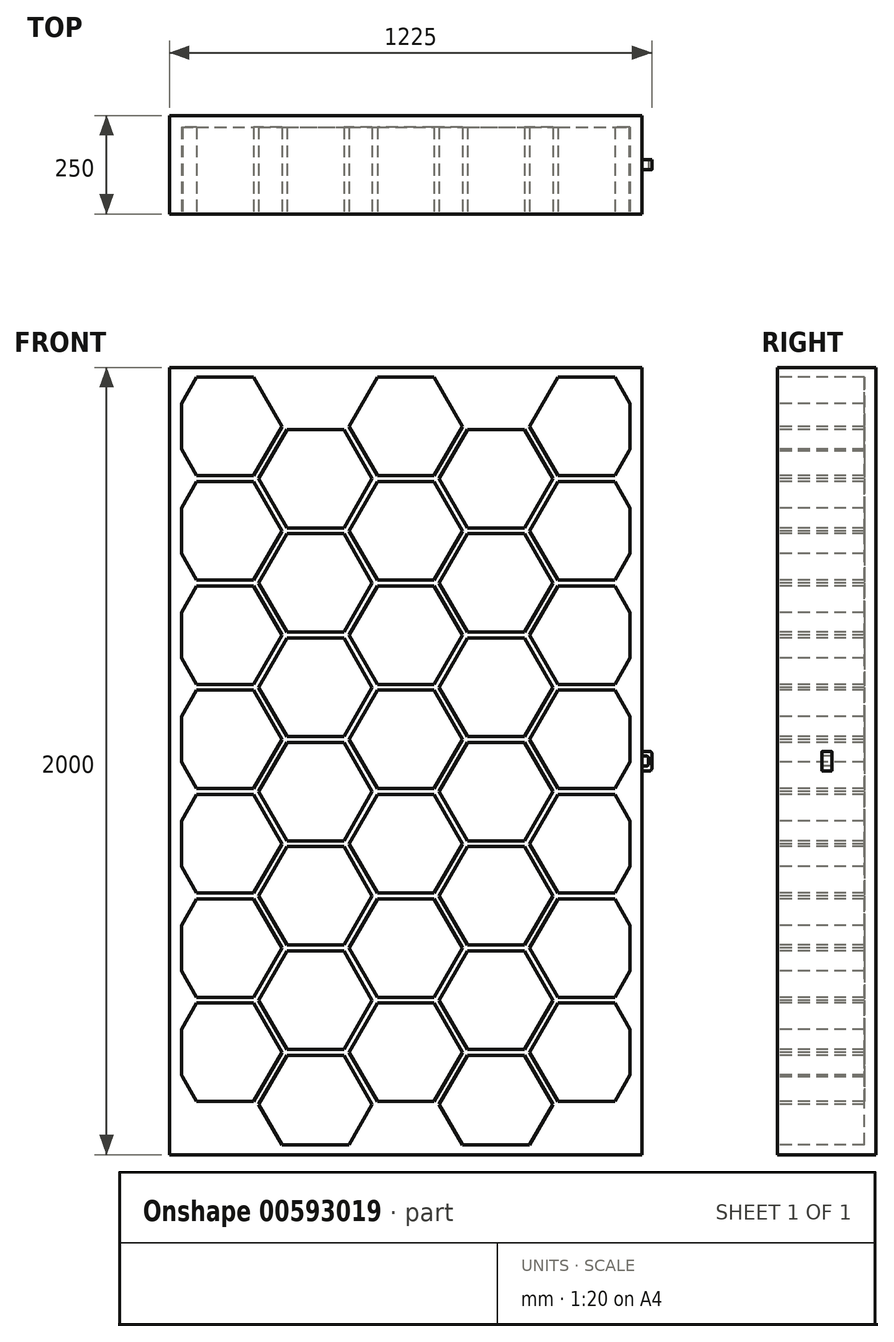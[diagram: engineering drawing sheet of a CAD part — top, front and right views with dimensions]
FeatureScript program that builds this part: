
annotation { "Feature Type Name" : "Feature", "Feature Type Description" : "" }
export const myFeature = defineFeature(function(context is Context, id is Id, definition is map)
    precondition{}
    {
        {
            var Q0;
            Q0=qCreatedBy(makeId("Top.planeOp"),FACE);
            var sketch = newSketch(context, id + "F0", { "sketchPlane" : qUnion([Q0])});
            skLineSegment(sketch, "E0.bottom", {"start": v(0, 0) * mm, "end": v(1200, 0) * mm});
            skLineSegment(sketch, "E0.top", {"start": v(0, 250) * mm, "end": v(1200, 250) * mm});
            skLineSegment(sketch, "E0.left", {"start": v(0, 0) * mm, "end": v(0, 250) * mm});
            skLineSegment(sketch, "E0.right", {"start": v(1200, 0) * mm, "end": v(1200, 250) * mm});
            skSolve(sketch);
        }
        {
            var Q0;
            Q0 = qSketchRegion(id + "F0", true);
            extrude(context, id + "F1", {"entities" : qUnion([Q0]), "depth" : 2000 * mm, "offsetDistance" : 25 * mm});
        }
        {
            var Q0;
            Q0=makeQuery(id+"F1.opExtrude","CAP_FACE",FACE,{"disambiguationData":[OSD([sQuery(id+"F0.wireOp",EDGE,"E0.bottom"),sQuery(id+"F0.wireOp",EDGE,"E0.top"),sQuery(id+"F0.wireOp",EDGE,"E0.left"),sQuery(id+"F0.wireOp",EDGE,"E0.right")])],"isStart":false});
            cPlane(context, id + "F2", {"entities" : qUnion([Q0]), "cplaneType" : CPlaneType.OFFSET, "offset" : 1000 * mm, "oppositeDirection" : true, "width" : 150 * mm, "height" : 150 * mm});
        }
        {
            var Q0;
            Q0=makeQuery(id+"F1.opExtrude","SWEPT_FACE",FACE,{"disambiguationData":[OSD([sQuery(id+"F0.wireOp",EDGE,"E0.left")])]});
            cPlane(context, id + "F3", {"entities" : qUnion([Q0]), "cplaneType" : CPlaneType.OFFSET, "offset" : 600 * mm, "oppositeDirection" : true, "width" : 150 * mm, "height" : 150 * mm});
        }
        {
            var Q0;
            Q0=makeQuery(id+"F1.opExtrude","SWEPT_FACE",FACE,{"disambiguationData":[OSD([sQuery(id+"F0.wireOp",EDGE,"E0.bottom")])]});
            var sketch = newSketch(context, id + "F4", { "sketchPlane" : qUnion([Q0])});
            skCircle(sketch, "E1.cCircle", {"center": v(600, 1850) * mm, "radius": 125 * mm, "construction": true});
            skLineSegment(sketch, "E1.0", {"start": v(744.34, 1850) * mm, "end": v(672.17, 1725) * mm});
            skLineSegment(sketch, "E1.1", {"start": v(672.17, 1725) * mm, "end": v(527.83, 1725) * mm});
            skLineSegment(sketch, "E1.2", {"start": v(527.83, 1725) * mm, "end": v(455.66, 1850) * mm});
            skLineSegment(sketch, "E1.3", {"start": v(455.66, 1850) * mm, "end": v(527.83, 1975) * mm});
            skLineSegment(sketch, "E1.4", {"start": v(527.83, 1975) * mm, "end": v(672.17, 1975) * mm});
            skLineSegment(sketch, "E1.5", {"start": v(672.17, 1975) * mm, "end": v(744.34, 1850) * mm});
            skPoint(sketch, "E1.0.midPoint", {"position": v(708.25, 1787.5) * mm});
            skCircle(sketch, "E2.cCircle", {"center": v(829.5, 1717.5) * mm, "radius": 125 * mm, "construction": true});
            skLineSegment(sketch, "E2.0", {"start": v(973.83, 1717.5) * mm, "end": v(901.67, 1592.5) * mm});
            skLineSegment(sketch, "E2.1", {"start": v(901.67, 1592.5) * mm, "end": v(757.33, 1592.5) * mm});
            skLineSegment(sketch, "E2.2", {"start": v(757.33, 1592.5) * mm, "end": v(685.16, 1717.5) * mm});
            skLineSegment(sketch, "E2.3", {"start": v(685.16, 1717.5) * mm, "end": v(757.33, 1842.5) * mm});
            skLineSegment(sketch, "E2.4", {"start": v(757.33, 1842.5) * mm, "end": v(901.67, 1842.5) * mm});
            skLineSegment(sketch, "E2.5", {"start": v(901.67, 1842.5) * mm, "end": v(973.83, 1717.5) * mm});
            skPoint(sketch, "E2.0.midPoint", {"position": v(937.75, 1655) * mm});
            skCircle(sketch, "E3.cCircle", {"center": v(600, 1585) * mm, "radius": 125 * mm, "construction": true});
            skLineSegment(sketch, "E3.0", {"start": v(744.34, 1585) * mm, "end": v(672.17, 1460) * mm});
            skLineSegment(sketch, "E3.1", {"start": v(672.17, 1460) * mm, "end": v(527.83, 1460) * mm});
            skLineSegment(sketch, "E3.2", {"start": v(527.83, 1460) * mm, "end": v(455.66, 1585) * mm});
            skLineSegment(sketch, "E3.3", {"start": v(455.66, 1585) * mm, "end": v(527.83, 1710) * mm});
            skLineSegment(sketch, "E3.4", {"start": v(527.83, 1710) * mm, "end": v(672.17, 1710) * mm});
            skLineSegment(sketch, "E3.5", {"start": v(672.17, 1710) * mm, "end": v(744.34, 1585) * mm});
            skPoint(sketch, "E3.0.midPoint", {"position": v(708.25, 1522.5) * mm});
            skCircle(sketch, "E4.cCircle", {"center": v(370.5, 1717.5) * mm, "radius": 125 * mm, "construction": true});
            skLineSegment(sketch, "E4.0", {"start": v(514.84, 1717.5) * mm, "end": v(442.67, 1592.5) * mm});
            skLineSegment(sketch, "E4.1", {"start": v(442.67, 1592.5) * mm, "end": v(298.33, 1592.5) * mm});
            skLineSegment(sketch, "E4.2", {"start": v(298.33, 1592.5) * mm, "end": v(226.17, 1717.5) * mm});
            skLineSegment(sketch, "E4.3", {"start": v(226.17, 1717.5) * mm, "end": v(298.33, 1842.5) * mm});
            skLineSegment(sketch, "E4.4", {"start": v(298.33, 1842.5) * mm, "end": v(442.67, 1842.5) * mm});
            skLineSegment(sketch, "E4.5", {"start": v(442.67, 1842.5) * mm, "end": v(514.84, 1717.5) * mm});
            skPoint(sketch, "E4.0.midPoint", {"position": v(478.76, 1655) * mm});
            skCircle(sketch, "E5.cCircle", {"center": v(370.5, 1452.5) * mm, "radius": 125 * mm, "construction": true});
            skLineSegment(sketch, "E5.0", {"start": v(514.84, 1452.5) * mm, "end": v(442.67, 1327.5) * mm});
            skLineSegment(sketch, "E5.1", {"start": v(442.67, 1327.5) * mm, "end": v(298.33, 1327.5) * mm});
            skLineSegment(sketch, "E5.2", {"start": v(298.33, 1327.5) * mm, "end": v(226.17, 1452.5) * mm});
            skLineSegment(sketch, "E5.3", {"start": v(226.17, 1452.5) * mm, "end": v(298.33, 1577.5) * mm});
            skLineSegment(sketch, "E5.4", {"start": v(298.33, 1577.5) * mm, "end": v(442.67, 1577.5) * mm});
            skLineSegment(sketch, "E5.5", {"start": v(442.67, 1577.5) * mm, "end": v(514.84, 1452.5) * mm});
            skPoint(sketch, "E5.0.midPoint", {"position": v(478.76, 1390) * mm});
            skArc(sketch, "E6.cCircle", {"start": v(30, 1527.53) * mm, "mid": v(265.97, 1582.13) * mm, "end": v(32.75, 1647.5) * mm, "construction": true});
            skLineSegment(sketch, "E6.0", {"start": v(213.18, 1460) * mm, "end": v(68.84, 1460) * mm});
            skLineSegment(sketch, "E6.1", {"start": v(68.84, 1460) * mm, "end": v(30, 1527.27) * mm});
            skLineSegment(sketch, "E6.2", {"start": v(30, 1642.73) * mm, "end": v(68.84, 1710) * mm});
            skLineSegment(sketch, "E6.3", {"start": v(68.84, 1710) * mm, "end": v(213.18, 1710) * mm});
            skLineSegment(sketch, "E6.4", {"start": v(213.18, 1710) * mm, "end": v(285.34, 1585) * mm});
            skLineSegment(sketch, "E6.5", {"start": v(285.34, 1585) * mm, "end": v(213.18, 1460) * mm});
            skArc(sketch, "E7.cCircle", {"start": v(1170, 1642.47) * mm, "mid": v(934, 1585) * mm, "end": v(1170, 1527.53) * mm, "construction": true});
            skLineSegment(sketch, "E7.0", {"start": v(1170, 1527.27) * mm, "end": v(1131.16, 1460) * mm});
            skLineSegment(sketch, "E7.1", {"start": v(1131.16, 1460) * mm, "end": v(986.82, 1460) * mm});
            skLineSegment(sketch, "E7.2", {"start": v(986.82, 1460) * mm, "end": v(914.66, 1585) * mm});
            skLineSegment(sketch, "E7.3", {"start": v(914.66, 1585) * mm, "end": v(986.82, 1710) * mm});
            skLineSegment(sketch, "E7.4", {"start": v(986.82, 1710) * mm, "end": v(1131.16, 1710) * mm});
            skLineSegment(sketch, "E7.5", {"start": v(1131.16, 1710) * mm, "end": v(1170, 1642.73) * mm});
            skPoint(sketch, "E7.0.midPoint", {"position": v(1167.25, 1522.5) * mm});
            skArc(sketch, "E8.cCircle", {"start": v(1170, 1377.47) * mm, "mid": v(934, 1320) * mm, "end": v(1170, 1262.53) * mm, "construction": true});
            skLineSegment(sketch, "E8.0", {"start": v(1170, 1262.27) * mm, "end": v(1131.16, 1195) * mm});
            skLineSegment(sketch, "E8.1", {"start": v(1131.16, 1195) * mm, "end": v(986.82, 1195) * mm});
            skLineSegment(sketch, "E8.2", {"start": v(986.82, 1195) * mm, "end": v(914.66, 1320) * mm});
            skLineSegment(sketch, "E8.3", {"start": v(914.66, 1320) * mm, "end": v(986.82, 1445) * mm});
            skLineSegment(sketch, "E8.4", {"start": v(986.82, 1445) * mm, "end": v(1131.16, 1445) * mm});
            skLineSegment(sketch, "E8.5", {"start": v(1131.16, 1445) * mm, "end": v(1170, 1377.73) * mm});
            skPoint(sketch, "E8.0.midPoint", {"position": v(1167.25, 1257.5) * mm});
            skCircle(sketch, "E9.cCircle", {"center": v(829.5, 1452.5) * mm, "radius": 125 * mm, "construction": true});
            skLineSegment(sketch, "E9.0", {"start": v(973.83, 1452.5) * mm, "end": v(901.67, 1327.5) * mm});
            skLineSegment(sketch, "E9.1", {"start": v(901.67, 1327.5) * mm, "end": v(757.33, 1327.5) * mm});
            skLineSegment(sketch, "E9.2", {"start": v(757.33, 1327.5) * mm, "end": v(685.16, 1452.5) * mm});
            skLineSegment(sketch, "E9.3", {"start": v(685.16, 1452.5) * mm, "end": v(757.33, 1577.5) * mm});
            skLineSegment(sketch, "E9.4", {"start": v(757.33, 1577.5) * mm, "end": v(901.67, 1577.5) * mm});
            skLineSegment(sketch, "E9.5", {"start": v(901.67, 1577.5) * mm, "end": v(973.83, 1452.5) * mm});
            skPoint(sketch, "E9.0.midPoint", {"position": v(937.75, 1390) * mm});
            skCircle(sketch, "E10.cCircle", {"center": v(829.5, 1187.5) * mm, "radius": 125 * mm, "construction": true});
            skLineSegment(sketch, "E10.0", {"start": v(973.83, 1187.5) * mm, "end": v(901.67, 1062.5) * mm});
            skLineSegment(sketch, "E10.1", {"start": v(901.67, 1062.5) * mm, "end": v(757.33, 1062.5) * mm});
            skLineSegment(sketch, "E10.2", {"start": v(757.33, 1062.5) * mm, "end": v(685.16, 1187.5) * mm});
            skLineSegment(sketch, "E10.3", {"start": v(685.16, 1187.5) * mm, "end": v(757.33, 1312.5) * mm});
            skLineSegment(sketch, "E10.4", {"start": v(757.33, 1312.5) * mm, "end": v(901.67, 1312.5) * mm});
            skLineSegment(sketch, "E10.5", {"start": v(901.67, 1312.5) * mm, "end": v(973.83, 1187.5) * mm});
            skPoint(sketch, "E10.0.midPoint", {"position": v(937.75, 1125) * mm});
            skCircle(sketch, "E11.cCircle", {"center": v(600, 1320) * mm, "radius": 125 * mm, "construction": true});
            skLineSegment(sketch, "E11.0", {"start": v(672.17, 1195) * mm, "end": v(527.83, 1195) * mm});
            skLineSegment(sketch, "E11.1", {"start": v(527.83, 1195) * mm, "end": v(455.66, 1320) * mm});
            skLineSegment(sketch, "E11.2", {"start": v(455.66, 1320) * mm, "end": v(527.83, 1445) * mm});
            skLineSegment(sketch, "E11.3", {"start": v(527.83, 1445) * mm, "end": v(672.17, 1445) * mm});
            skLineSegment(sketch, "E11.4", {"start": v(672.17, 1445) * mm, "end": v(744.34, 1320) * mm});
            skLineSegment(sketch, "E11.5", {"start": v(744.34, 1320) * mm, "end": v(672.17, 1195) * mm});
            skPoint(sketch, "E11.0.midPoint", {"position": v(600, 1195) * mm});
            skArc(sketch, "E12.cCircle", {"start": v(32.75, 1257.5) * mm, "mid": v(265.97, 1322.87) * mm, "end": v(30, 1377.47) * mm, "construction": true});
            skLineSegment(sketch, "E12.0", {"start": v(213.18, 1445) * mm, "end": v(285.34, 1320) * mm});
            skLineSegment(sketch, "E12.1", {"start": v(285.34, 1320) * mm, "end": v(213.18, 1195) * mm});
            skLineSegment(sketch, "E12.2", {"start": v(213.18, 1195) * mm, "end": v(68.84, 1195) * mm});
            skLineSegment(sketch, "E12.3", {"start": v(68.84, 1195) * mm, "end": v(30, 1262.27) * mm});
            skLineSegment(sketch, "E12.4", {"start": v(30, 1377.73) * mm, "end": v(68.84, 1445) * mm});
            skLineSegment(sketch, "E12.5", {"start": v(68.84, 1445) * mm, "end": v(213.18, 1445) * mm});
            skPoint(sketch, "E12.0.midPoint", {"position": v(249.26, 1382.5) * mm});
            skPoint(sketch, "E13.0.midPoint", {"position": v(472.1, 1108.47) * mm});
            skLineSegment(sketch, "E14", {"start": v(1170, 1642.73) * mm, "end": v(1170, 1527.27) * mm});
            skLineSegment(sketch, "E15", {"start": v(30, 1642.73) * mm, "end": v(30, 1527.27) * mm});
            skPoint(sketch, "E16.orphan", {"position": v(1203.33, 1585) * mm});
            skLineSegment(sketch, "E17.trimOffspring", {"start": v(1170, 1377.73) * mm, "end": v(1170, 1262.27) * mm});
            skPoint(sketch, "E18.orphan", {"position": v(1203.33, 1320) * mm});
            skPoint(sketch, "E19.orphan", {"position": v(-3.33, 1320) * mm});
            skPoint(sketch, "E20.orphan", {"position": v(-3.33, 1585) * mm});
            skLineSegment(sketch, "E21.trimOffspring", {"start": v(30, 1377.73) * mm, "end": v(30, 1262.27) * mm});
            skPoint(sketch, "E22.orphan", {"position": v(508.18, 1170.97) * mm});
            skPoint(sketch, "E13.0.end.orphan", {"position": v(436.01, 1045.97) * mm});
            skSolve(sketch);
        }
        {
            var Q0;
            Q0 = qSketchRegion(id + "F4", true);
            extrude(context, id + "F5", {"entities" : qUnion([Q0]), "operationType" : NewBodyOperationType.REMOVE, "oppositeDirection" : true, "depth" : 220 * mm, "offsetDistance" : 25 * mm});
        }
        {
            var Q0;
            Q0=makeQuery(id+"F1.opExtrude","SWEPT_FACE",FACE,{"disambiguationData":[OSD([sQuery(id+"F0.wireOp",EDGE,"E0.bottom")])]});
            var sketch = newSketch(context, id + "F6", { "sketchPlane" : qUnion([Q0])});
            skCircle(sketch, "E23.cCircle", {"center": v(370.5, 1187.5) * mm, "radius": 125 * mm, "construction": true});
            skLineSegment(sketch, "E23.0", {"start": v(514.84, 1187.5) * mm, "end": v(442.67, 1062.5) * mm});
            skLineSegment(sketch, "E23.1", {"start": v(442.67, 1062.5) * mm, "end": v(298.33, 1062.5) * mm});
            skLineSegment(sketch, "E23.2", {"start": v(298.33, 1062.5) * mm, "end": v(226.17, 1187.5) * mm});
            skLineSegment(sketch, "E23.3", {"start": v(226.17, 1187.5) * mm, "end": v(298.33, 1312.5) * mm});
            skLineSegment(sketch, "E23.4", {"start": v(298.33, 1312.5) * mm, "end": v(442.67, 1312.5) * mm});
            skLineSegment(sketch, "E23.5", {"start": v(442.67, 1312.5) * mm, "end": v(514.84, 1187.5) * mm});
            skPoint(sketch, "E23.0.midPoint", {"position": v(478.76, 1125) * mm});
            skCircle(sketch, "E24.cCircle", {"center": v(600, 1055) * mm, "radius": 125 * mm, "construction": true});
            skLineSegment(sketch, "E24.0", {"start": v(744.34, 1055) * mm, "end": v(672.17, 930) * mm});
            skLineSegment(sketch, "E24.1", {"start": v(672.17, 930) * mm, "end": v(527.83, 930) * mm});
            skLineSegment(sketch, "E24.2", {"start": v(527.83, 930) * mm, "end": v(455.66, 1055) * mm});
            skLineSegment(sketch, "E24.3", {"start": v(455.66, 1055) * mm, "end": v(527.83, 1180) * mm});
            skLineSegment(sketch, "E24.4", {"start": v(527.83, 1180) * mm, "end": v(672.17, 1180) * mm});
            skLineSegment(sketch, "E24.5", {"start": v(672.17, 1180) * mm, "end": v(744.34, 1055) * mm});
            skPoint(sketch, "E24.0.midPoint", {"position": v(708.25, 992.5) * mm});
            skArc(sketch, "E25.cCircle", {"start": v(30, 997.53) * mm, "mid": v(266, 1055) * mm, "end": v(30, 1112.47) * mm, "construction": true});
            skLineSegment(sketch, "E25.0", {"start": v(285.34, 1055) * mm, "end": v(213.18, 930) * mm});
            skLineSegment(sketch, "E25.1", {"start": v(213.18, 930) * mm, "end": v(68.84, 930) * mm});
            skLineSegment(sketch, "E25.2", {"start": v(68.84, 930) * mm, "end": v(30, 997.27) * mm});
            skLineSegment(sketch, "E25.3", {"start": v(30, 1112.73) * mm, "end": v(68.84, 1180) * mm});
            skLineSegment(sketch, "E25.4", {"start": v(68.84, 1180) * mm, "end": v(213.18, 1180) * mm});
            skLineSegment(sketch, "E25.5", {"start": v(213.18, 1180) * mm, "end": v(285.34, 1055) * mm});
            skPoint(sketch, "E25.0.midPoint", {"position": v(249.26, 992.5) * mm});
            skArc(sketch, "E26.cCircle", {"start": v(1170, 1112.47) * mm, "mid": v(934, 1055) * mm, "end": v(1170, 997.53) * mm, "construction": true});
            skLineSegment(sketch, "E26.0", {"start": v(1170, 997.27) * mm, "end": v(1131.16, 930) * mm});
            skLineSegment(sketch, "E26.1", {"start": v(1131.16, 930) * mm, "end": v(986.82, 930) * mm});
            skLineSegment(sketch, "E26.2", {"start": v(986.82, 930) * mm, "end": v(914.66, 1055) * mm});
            skLineSegment(sketch, "E26.3", {"start": v(914.66, 1055) * mm, "end": v(986.82, 1180) * mm});
            skLineSegment(sketch, "E26.4", {"start": v(986.82, 1180) * mm, "end": v(1131.16, 1180) * mm});
            skLineSegment(sketch, "E26.5", {"start": v(1131.16, 1180) * mm, "end": v(1170, 1112.73) * mm});
            skPoint(sketch, "E26.0.midPoint", {"position": v(1167.25, 992.5) * mm});
            skCircle(sketch, "E27.cCircle", {"center": v(829.5, 922.5) * mm, "radius": 125 * mm, "construction": true});
            skLineSegment(sketch, "E27.0", {"start": v(973.83, 922.5) * mm, "end": v(901.67, 797.5) * mm});
            skLineSegment(sketch, "E27.1", {"start": v(901.67, 797.5) * mm, "end": v(757.33, 797.5) * mm});
            skLineSegment(sketch, "E27.2", {"start": v(757.33, 797.5) * mm, "end": v(685.16, 922.5) * mm});
            skLineSegment(sketch, "E27.3", {"start": v(685.16, 922.5) * mm, "end": v(757.33, 1047.5) * mm});
            skLineSegment(sketch, "E27.4", {"start": v(757.33, 1047.5) * mm, "end": v(901.67, 1047.5) * mm});
            skLineSegment(sketch, "E27.5", {"start": v(901.67, 1047.5) * mm, "end": v(973.83, 922.5) * mm});
            skPoint(sketch, "E27.0.midPoint", {"position": v(937.75, 860) * mm});
            skCircle(sketch, "E28.cCircle", {"center": v(370.5, 922.5) * mm, "radius": 125 * mm, "construction": true});
            skLineSegment(sketch, "E28.0", {"start": v(514.84, 922.5) * mm, "end": v(442.67, 797.5) * mm});
            skLineSegment(sketch, "E28.1", {"start": v(442.67, 797.5) * mm, "end": v(298.33, 797.5) * mm});
            skLineSegment(sketch, "E28.2", {"start": v(298.33, 797.5) * mm, "end": v(226.17, 922.5) * mm});
            skLineSegment(sketch, "E28.3", {"start": v(226.17, 922.5) * mm, "end": v(298.33, 1047.5) * mm});
            skLineSegment(sketch, "E28.4", {"start": v(298.33, 1047.5) * mm, "end": v(442.67, 1047.5) * mm});
            skLineSegment(sketch, "E28.5", {"start": v(442.67, 1047.5) * mm, "end": v(514.84, 922.5) * mm});
            skPoint(sketch, "E28.0.midPoint", {"position": v(478.76, 860) * mm});
            skArc(sketch, "E29.cCircle", {"start": v(30, 732.53) * mm, "mid": v(266, 790) * mm, "end": v(30, 847.47) * mm, "construction": true});
            skLineSegment(sketch, "E29.0", {"start": v(285.34, 790) * mm, "end": v(213.18, 665) * mm});
            skLineSegment(sketch, "E29.1", {"start": v(213.18, 665) * mm, "end": v(68.84, 665) * mm});
            skLineSegment(sketch, "E29.2", {"start": v(68.84, 665) * mm, "end": v(30, 732.27) * mm});
            skLineSegment(sketch, "E29.3", {"start": v(30, 847.73) * mm, "end": v(68.84, 915) * mm});
            skLineSegment(sketch, "E29.4", {"start": v(68.84, 915) * mm, "end": v(213.18, 915) * mm});
            skLineSegment(sketch, "E29.5", {"start": v(213.18, 915) * mm, "end": v(285.34, 790) * mm});
            skPoint(sketch, "E29.0.midPoint", {"position": v(249.26, 727.5) * mm});
            skCircle(sketch, "E30.cCircle", {"center": v(600, 790) * mm, "radius": 125 * mm, "construction": true});
            skLineSegment(sketch, "E30.0", {"start": v(744.34, 790) * mm, "end": v(672.17, 665) * mm});
            skLineSegment(sketch, "E30.1", {"start": v(672.17, 665) * mm, "end": v(527.83, 665) * mm});
            skLineSegment(sketch, "E30.2", {"start": v(527.83, 665) * mm, "end": v(455.66, 790) * mm});
            skLineSegment(sketch, "E30.3", {"start": v(455.66, 790) * mm, "end": v(527.83, 915) * mm});
            skLineSegment(sketch, "E30.4", {"start": v(527.83, 915) * mm, "end": v(672.17, 915) * mm});
            skLineSegment(sketch, "E30.5", {"start": v(672.17, 915) * mm, "end": v(744.34, 790) * mm});
            skPoint(sketch, "E30.0.midPoint", {"position": v(708.25, 727.5) * mm});
            skCircle(sketch, "E31.cCircle", {"center": v(829.5, 657.5) * mm, "radius": 125 * mm, "construction": true});
            skLineSegment(sketch, "E31.0", {"start": v(973.83, 657.5) * mm, "end": v(901.67, 532.5) * mm});
            skLineSegment(sketch, "E31.1", {"start": v(901.67, 532.5) * mm, "end": v(757.33, 532.5) * mm});
            skLineSegment(sketch, "E31.2", {"start": v(757.33, 532.5) * mm, "end": v(685.16, 657.5) * mm});
            skLineSegment(sketch, "E31.3", {"start": v(685.16, 657.5) * mm, "end": v(757.33, 782.5) * mm});
            skLineSegment(sketch, "E31.4", {"start": v(757.33, 782.5) * mm, "end": v(901.67, 782.5) * mm});
            skLineSegment(sketch, "E31.5", {"start": v(901.67, 782.5) * mm, "end": v(973.83, 657.5) * mm});
            skPoint(sketch, "E31.0.midPoint", {"position": v(937.75, 595) * mm});
            skArc(sketch, "E32.cCircle", {"start": v(1170, 847.47) * mm, "mid": v(934, 790) * mm, "end": v(1170, 732.53) * mm, "construction": true});
            skLineSegment(sketch, "E32.0", {"start": v(1170, 732.27) * mm, "end": v(1131.16, 665) * mm});
            skLineSegment(sketch, "E32.1", {"start": v(1131.16, 665) * mm, "end": v(986.82, 665) * mm});
            skLineSegment(sketch, "E32.2", {"start": v(986.82, 665) * mm, "end": v(914.66, 790) * mm});
            skLineSegment(sketch, "E32.3", {"start": v(914.66, 790) * mm, "end": v(986.82, 915) * mm});
            skLineSegment(sketch, "E32.4", {"start": v(986.82, 915) * mm, "end": v(1131.16, 915) * mm});
            skLineSegment(sketch, "E32.5", {"start": v(1131.16, 915) * mm, "end": v(1170, 847.73) * mm});
            skPoint(sketch, "E32.0.midPoint", {"position": v(1167.25, 727.5) * mm});
            skCircle(sketch, "E33.cCircle", {"center": v(370.5, 657.5) * mm, "radius": 125 * mm, "construction": true});
            skLineSegment(sketch, "E33.0", {"start": v(514.84, 657.5) * mm, "end": v(442.67, 532.5) * mm});
            skLineSegment(sketch, "E33.1", {"start": v(442.67, 532.5) * mm, "end": v(298.33, 532.5) * mm});
            skLineSegment(sketch, "E33.2", {"start": v(298.33, 532.5) * mm, "end": v(226.17, 657.5) * mm});
            skLineSegment(sketch, "E33.3", {"start": v(226.17, 657.5) * mm, "end": v(298.33, 782.5) * mm});
            skLineSegment(sketch, "E33.4", {"start": v(298.33, 782.5) * mm, "end": v(442.67, 782.5) * mm});
            skLineSegment(sketch, "E33.5", {"start": v(442.67, 782.5) * mm, "end": v(514.84, 657.5) * mm});
            skPoint(sketch, "E33.0.midPoint", {"position": v(478.76, 595) * mm});
            skArc(sketch, "E34.cCircle", {"start": v(30, 467.53) * mm, "mid": v(266, 525) * mm, "end": v(30, 582.47) * mm, "construction": true});
            skLineSegment(sketch, "E34.0", {"start": v(285.34, 525) * mm, "end": v(213.18, 400) * mm});
            skLineSegment(sketch, "E34.1", {"start": v(213.18, 400) * mm, "end": v(68.84, 400) * mm});
            skLineSegment(sketch, "E34.2", {"start": v(68.84, 400) * mm, "end": v(30, 467.27) * mm});
            skLineSegment(sketch, "E34.3", {"start": v(30, 582.73) * mm, "end": v(68.84, 650) * mm});
            skLineSegment(sketch, "E34.4", {"start": v(68.84, 650) * mm, "end": v(213.18, 650) * mm});
            skLineSegment(sketch, "E34.5", {"start": v(213.18, 650) * mm, "end": v(285.34, 525) * mm});
            skPoint(sketch, "E34.0.midPoint", {"position": v(249.26, 462.5) * mm});
            skCircle(sketch, "E35.cCircle", {"center": v(370.5, 392.5) * mm, "radius": 125 * mm, "construction": true});
            skLineSegment(sketch, "E35.0", {"start": v(514.84, 392.5) * mm, "end": v(442.67, 267.5) * mm});
            skLineSegment(sketch, "E35.1", {"start": v(442.67, 267.5) * mm, "end": v(298.33, 267.5) * mm});
            skLineSegment(sketch, "E35.2", {"start": v(298.33, 267.5) * mm, "end": v(226.17, 392.5) * mm});
            skLineSegment(sketch, "E35.3", {"start": v(226.17, 392.5) * mm, "end": v(298.33, 517.5) * mm});
            skLineSegment(sketch, "E35.4", {"start": v(298.33, 517.5) * mm, "end": v(442.67, 517.5) * mm});
            skLineSegment(sketch, "E35.5", {"start": v(442.67, 517.5) * mm, "end": v(514.84, 392.5) * mm});
            skPoint(sketch, "E35.0.midPoint", {"position": v(478.76, 330) * mm});
            skCircle(sketch, "E36.cCircle", {"center": v(600, 525) * mm, "radius": 125 * mm, "construction": true});
            skLineSegment(sketch, "E36.0", {"start": v(744.34, 525) * mm, "end": v(672.17, 400) * mm});
            skLineSegment(sketch, "E36.1", {"start": v(672.17, 400) * mm, "end": v(527.83, 400) * mm});
            skLineSegment(sketch, "E36.2", {"start": v(527.83, 400) * mm, "end": v(455.66, 525) * mm});
            skLineSegment(sketch, "E36.3", {"start": v(455.66, 525) * mm, "end": v(527.83, 650) * mm});
            skLineSegment(sketch, "E36.4", {"start": v(527.83, 650) * mm, "end": v(672.17, 650) * mm});
            skLineSegment(sketch, "E36.5", {"start": v(672.17, 650) * mm, "end": v(744.34, 525) * mm});
            skPoint(sketch, "E36.0.midPoint", {"position": v(708.25, 462.5) * mm});
            skCircle(sketch, "E37.cCircle", {"center": v(829.5, 392.5) * mm, "radius": 125 * mm, "construction": true});
            skLineSegment(sketch, "E37.0", {"start": v(973.83, 392.5) * mm, "end": v(901.67, 267.5) * mm});
            skLineSegment(sketch, "E37.1", {"start": v(901.67, 267.5) * mm, "end": v(757.33, 267.5) * mm});
            skLineSegment(sketch, "E37.2", {"start": v(757.33, 267.5) * mm, "end": v(685.16, 392.5) * mm});
            skLineSegment(sketch, "E37.3", {"start": v(685.16, 392.5) * mm, "end": v(757.33, 517.5) * mm});
            skLineSegment(sketch, "E37.4", {"start": v(757.33, 517.5) * mm, "end": v(901.67, 517.5) * mm});
            skLineSegment(sketch, "E37.5", {"start": v(901.67, 517.5) * mm, "end": v(973.83, 392.5) * mm});
            skPoint(sketch, "E37.0.midPoint", {"position": v(937.75, 330) * mm});
            skArc(sketch, "E38.cCircle", {"start": v(1170, 582.47) * mm, "mid": v(934, 525) * mm, "end": v(1170, 467.53) * mm, "construction": true});
            skLineSegment(sketch, "E38.0", {"start": v(1170, 467.27) * mm, "end": v(1131.16, 400) * mm});
            skLineSegment(sketch, "E38.1", {"start": v(1131.16, 400) * mm, "end": v(986.82, 400) * mm});
            skLineSegment(sketch, "E38.2", {"start": v(986.82, 400) * mm, "end": v(914.66, 525) * mm});
            skLineSegment(sketch, "E38.3", {"start": v(914.66, 525) * mm, "end": v(986.82, 650) * mm});
            skLineSegment(sketch, "E38.4", {"start": v(986.82, 650) * mm, "end": v(1131.16, 650) * mm});
            skLineSegment(sketch, "E38.5", {"start": v(1131.16, 650) * mm, "end": v(1170, 582.73) * mm});
            skPoint(sketch, "E38.0.midPoint", {"position": v(1167.25, 462.5) * mm});
            skArc(sketch, "E39.cCircle", {"start": v(30, 202.53) * mm, "mid": v(266, 260) * mm, "end": v(30, 317.47) * mm, "construction": true});
            skLineSegment(sketch, "E39.0", {"start": v(285.34, 260) * mm, "end": v(213.18, 135) * mm});
            skLineSegment(sketch, "E39.1", {"start": v(213.18, 135) * mm, "end": v(68.84, 135) * mm});
            skLineSegment(sketch, "E39.2", {"start": v(68.84, 135) * mm, "end": v(32.75, 197.5) * mm});
            skLineSegment(sketch, "E39.3", {"start": v(30, 317.73) * mm, "end": v(68.84, 385) * mm});
            skLineSegment(sketch, "E39.4", {"start": v(68.84, 385) * mm, "end": v(213.18, 385) * mm});
            skLineSegment(sketch, "E39.5", {"start": v(213.18, 385) * mm, "end": v(285.34, 260) * mm});
            skPoint(sketch, "E39.0.midPoint", {"position": v(249.26, 197.5) * mm});
            skArc(sketch, "E40.cCircle", {"start": v(442.05, 25) * mm, "mid": v(370.5, 252.5) * mm, "end": v(298.96, 25) * mm, "construction": true});
            skLineSegment(sketch, "E40.0", {"start": v(514.84, 127.5) * mm, "end": v(455.66, 25) * mm});
            skLineSegment(sketch, "E40.2", {"start": v(285.34, 25) * mm, "end": v(226.17, 127.5) * mm});
            skLineSegment(sketch, "E40.3", {"start": v(226.17, 127.5) * mm, "end": v(298.33, 252.5) * mm});
            skLineSegment(sketch, "E40.4", {"start": v(298.33, 252.5) * mm, "end": v(442.67, 252.5) * mm});
            skLineSegment(sketch, "E40.5", {"start": v(442.67, 252.5) * mm, "end": v(514.84, 127.5) * mm});
            skPoint(sketch, "E40.0.midPoint", {"position": v(478.76, 65) * mm});
            skCircle(sketch, "E41.cCircle", {"center": v(600, 260) * mm, "radius": 125 * mm, "construction": true});
            skLineSegment(sketch, "E41.0", {"start": v(744.34, 260) * mm, "end": v(672.17, 135) * mm});
            skLineSegment(sketch, "E41.1", {"start": v(672.17, 135) * mm, "end": v(527.83, 135) * mm});
            skLineSegment(sketch, "E41.2", {"start": v(527.83, 135) * mm, "end": v(455.66, 260) * mm});
            skLineSegment(sketch, "E41.3", {"start": v(455.66, 260) * mm, "end": v(527.83, 385) * mm});
            skLineSegment(sketch, "E41.4", {"start": v(527.83, 385) * mm, "end": v(672.17, 385) * mm});
            skLineSegment(sketch, "E41.5", {"start": v(672.17, 385) * mm, "end": v(744.34, 260) * mm});
            skPoint(sketch, "E41.0.midPoint", {"position": v(708.25, 197.5) * mm});
            skArc(sketch, "E42.cCircle", {"start": v(901.04, 25) * mm, "mid": v(829.5, 252.5) * mm, "end": v(757.95, 25) * mm, "construction": true});
            skLineSegment(sketch, "E42.0", {"start": v(973.83, 127.5) * mm, "end": v(914.66, 25) * mm});
            skLineSegment(sketch, "E42.2", {"start": v(744.34, 25) * mm, "end": v(685.16, 127.5) * mm});
            skLineSegment(sketch, "E42.3", {"start": v(685.16, 127.5) * mm, "end": v(757.33, 252.5) * mm});
            skLineSegment(sketch, "E42.4", {"start": v(757.33, 252.5) * mm, "end": v(901.67, 252.5) * mm});
            skLineSegment(sketch, "E42.5", {"start": v(901.67, 252.5) * mm, "end": v(973.83, 127.5) * mm});
            skPoint(sketch, "E42.0.midPoint", {"position": v(937.75, 65) * mm});
            skArc(sketch, "E43.cCircle", {"start": v(1170, 317.47) * mm, "mid": v(934, 260) * mm, "end": v(1170, 202.53) * mm, "construction": true});
            skLineSegment(sketch, "E43.0", {"start": v(1170, 202.27) * mm, "end": v(1131.16, 135) * mm});
            skLineSegment(sketch, "E43.1", {"start": v(1131.16, 135) * mm, "end": v(986.82, 135) * mm});
            skLineSegment(sketch, "E43.2", {"start": v(986.82, 135) * mm, "end": v(914.66, 260) * mm});
            skLineSegment(sketch, "E43.3", {"start": v(914.66, 260) * mm, "end": v(986.82, 385) * mm});
            skLineSegment(sketch, "E43.4", {"start": v(986.82, 385) * mm, "end": v(1131.16, 385) * mm});
            skLineSegment(sketch, "E43.5", {"start": v(1131.16, 385) * mm, "end": v(1170, 317.73) * mm});
            skPoint(sketch, "E43.0.midPoint", {"position": v(1167.25, 197.5) * mm});
            skArc(sketch, "E44.cCircle", {"start": v(30, 1792.53) * mm, "mid": v(266, 1850) * mm, "end": v(30, 1907.47) * mm, "construction": true});
            skLineSegment(sketch, "E44.0", {"start": v(285.34, 1850) * mm, "end": v(213.18, 1725) * mm});
            skLineSegment(sketch, "E44.1", {"start": v(213.18, 1725) * mm, "end": v(68.84, 1725) * mm});
            skLineSegment(sketch, "E44.3", {"start": v(30, 1907.73) * mm, "end": v(68.84, 1975) * mm});
            skLineSegment(sketch, "E44.4", {"start": v(68.84, 1975) * mm, "end": v(213.18, 1975) * mm});
            skLineSegment(sketch, "E44.5", {"start": v(213.18, 1975) * mm, "end": v(285.34, 1850) * mm});
            skPoint(sketch, "E44.0.midPoint", {"position": v(249.26, 1787.5) * mm});
            skArc(sketch, "E45.cCircle", {"start": v(1170, 1907.47) * mm, "mid": v(934, 1850) * mm, "end": v(1170, 1792.53) * mm, "construction": true});
            skLineSegment(sketch, "E45.0", {"start": v(1167.25, 1787.5) * mm, "end": v(1131.16, 1725) * mm});
            skLineSegment(sketch, "E45.1", {"start": v(1131.16, 1725) * mm, "end": v(986.82, 1725) * mm});
            skLineSegment(sketch, "E45.2", {"start": v(986.82, 1725) * mm, "end": v(914.66, 1850) * mm});
            skLineSegment(sketch, "E45.3", {"start": v(914.66, 1850) * mm, "end": v(986.82, 1975) * mm});
            skLineSegment(sketch, "E45.4", {"start": v(986.82, 1975) * mm, "end": v(1131.16, 1975) * mm});
            skLineSegment(sketch, "E45.5", {"start": v(1131.16, 1975) * mm, "end": v(1170, 1907.73) * mm});
            skPoint(sketch, "E45.0.midPoint", {"position": v(1167.25, 1787.5) * mm});
            skLineSegment(sketch, "E46", {"start": v(30, 1792.53) * mm, "end": v(30, 1907.73) * mm});
            skLineSegment(sketch, "E47", {"start": v(30, 1112.73) * mm, "end": v(30, 997.27) * mm});
            skLineSegment(sketch, "E48", {"start": v(1170, 1112.73) * mm, "end": v(1170, 997.27) * mm});
            skLineSegment(sketch, "E49", {"start": v(1170, 1792.53) * mm, "end": v(1170, 1907.73) * mm});
            skPoint(sketch, "E50.orphan", {"position": v(-3.33, 1055) * mm});
            skPoint(sketch, "E51.orphan", {"position": v(-3.33, 1850) * mm});
            skPoint(sketch, "E52.orphan", {"position": v(-3.33, 260) * mm});
            skPoint(sketch, "E53.orphan", {"position": v(-3.33, 525) * mm});
            skPoint(sketch, "E54.orphan", {"position": v(-3.33, 790) * mm});
            skPoint(sketch, "E55.orphan", {"position": v(1203.33, 1055) * mm});
            skPoint(sketch, "E56.orphan", {"position": v(1203.33, 790) * mm});
            skPoint(sketch, "E57.orphan", {"position": v(1203.33, 525) * mm});
            skPoint(sketch, "E58.orphan", {"position": v(1203.33, 260) * mm});
            skPoint(sketch, "E59.orphan", {"position": v(1203.33, 1850) * mm});
            skLineSegment(sketch, "E60", {"start": v(285.34, 25) * mm, "end": v(455.66, 25) * mm});
            skPoint(sketch, "E61.orphan", {"position": v(442.67, 2.5) * mm});
            skPoint(sketch, "E62.orphan", {"position": v(757.33, 2.5) * mm});
            skPoint(sketch, "E63.orphan", {"position": v(901.67, 2.5) * mm});
            skLineSegment(sketch, "E64.trimOffspring", {"start": v(744.34, 25) * mm, "end": v(914.66, 25) * mm});
            skPoint(sketch, "E65.orphan", {"position": v(1170, 0) * mm});
            skPoint(sketch, "E66.orphan", {"position": v(30, 0) * mm});
            skLineSegment(sketch, "E67.trimOffspring", {"start": v(30, 317.73) * mm, "end": v(30, 202.53) * mm});
            skLineSegment(sketch, "E68.trimOffspring", {"start": v(30, 582.73) * mm, "end": v(30, 467.27) * mm});
            skLineSegment(sketch, "E69.trimOffspring", {"start": v(30, 847.73) * mm, "end": v(30, 732.27) * mm});
            skPoint(sketch, "E70.orphan", {"position": v(30, 1585) * mm});
            skLineSegment(sketch, "E71", {"start": v(30, 1792.53) * mm, "end": v(68.84, 1725) * mm});
            skPoint(sketch, "E72.orphan", {"position": v(30, 2000) * mm});
            skLineSegment(sketch, "E73.trimOffspring", {"start": v(1170, 317.73) * mm, "end": v(1170, 202.27) * mm});
            skLineSegment(sketch, "E74.trimOffspring", {"start": v(1170, 582.73) * mm, "end": v(1170, 467.27) * mm});
            skLineSegment(sketch, "E75.trimOffspring", {"start": v(1170, 847.73) * mm, "end": v(1170, 732.27) * mm});
            skPoint(sketch, "E76.orphan", {"position": v(1170, 1585) * mm});
            skLineSegment(sketch, "E77", {"start": v(30, 202.53) * mm, "end": v(32.75, 197.5) * mm});
            skLineSegment(sketch, "E78", {"start": v(1170, 1792.53) * mm, "end": v(1167.25, 1787.5) * mm});
            skSolve(sketch);
        }
        {
            var Q0;
            Q0 = qSketchRegion(id + "F6", true);
            extrude(context, id + "F7", {"entities" : qUnion([Q0]), "operationType" : NewBodyOperationType.REMOVE, "oppositeDirection" : true, "depth" : 220 * mm, "offsetDistance" : 25 * mm});
        }
        {
            var Q0;
            Q0=makeQuery(id+"F1.opExtrude","SWEPT_FACE",FACE,{"disambiguationData":[OSD([sQuery(id+"F0.wireOp",EDGE,"E0.right")])]});
            var sketch = newSketch(context, id + "F8", { "sketchPlane" : qUnion([Q0])});
            skLineSegment(sketch, "E79.bottom", {"start": v(112.5, 1025) * mm, "end": v(137.5, 1025) * mm});
            skLineSegment(sketch, "E79.top", {"start": v(112.5, 975) * mm, "end": v(137.5, 975) * mm});
            skLineSegment(sketch, "E79.left", {"start": v(112.5, 1025) * mm, "end": v(112.5, 975) * mm});
            skLineSegment(sketch, "E79.right", {"start": v(137.5, 1025) * mm, "end": v(137.5, 975) * mm});
            skSolve(sketch);
        }
        {
            var Q0;
            Q0 = qSketchRegion(id + "F8", true);
            extrude(context, id + "F9", {"entities" : qUnion([Q0]), "operationType" : NewBodyOperationType.ADD, "depth" : 25 * mm, "offsetDistance" : 25 * mm});
        }
        {
            var Q0;
            Q0=makeQuery(id+"F9.opExtrude","SWEPT_FACE",FACE,{"disambiguationData":[OSD([sQuery(id+"F8.wireOp",EDGE,"E79.left")])]});
            var sketch = newSketch(context, id + "F10", { "sketchPlane" : qUnion([Q0])});
            skLineSegment(sketch, "E80.bottom", {"start": v(1200, 1012.5) * mm, "end": v(1217, 1012.5) * mm});
            skLineSegment(sketch, "E80.top", {"start": v(1200, 987.5) * mm, "end": v(1217, 987.5) * mm});
            skLineSegment(sketch, "E80.left", {"start": v(1200, 1012.5) * mm, "end": v(1200, 987.5) * mm});
            skLineSegment(sketch, "E80.right", {"start": v(1217, 1012.5) * mm, "end": v(1217, 987.5) * mm});
            skSolve(sketch);
        }
        {
            var Q0;
            Q0 = qSketchRegion(id + "F10", true);
            extrude(context, id + "F11", {"entities" : qUnion([Q0]), "operationType" : NewBodyOperationType.REMOVE, "oppositeDirection" : true, "depth" : 25 * mm, "offsetDistance" : 25 * mm});
        }
        {
            var Q0;
            Q0=makeQuery(id+"F9.opExtrude","CAP_EDGE",EDGE,{"disambiguationData":[OSD([sQuery(id+"F8.wireOp",EDGE,"E79.top")])],"isStart":false});
            var Q1;
            Q1=makeQuery(id+"F9.opExtrude","CAP_EDGE",EDGE,{"disambiguationData":[OSD([sQuery(id+"F8.wireOp",EDGE,"E79.bottom")])],"isStart":false});
            var Q2;
            Q2=makeQuery(id+"F11.boolean.opBoolean","COPY",EDGE,{"derivedFrom":makeQuery(id+"F11.opExtrude","SWEPT_EDGE",EDGE,{"disambiguationData":[OSD([sQuery(id+"F10.wireOp",EDGE,"E80.bottom"),sQuery(id+"F10.wireOp",EDGE,"E80.right")])]})});
            var Q3;
            Q3=makeQuery(id+"F11.boolean.opBoolean","COPY",EDGE,{"derivedFrom":makeQuery(id+"F11.opExtrude","SWEPT_EDGE",EDGE,{"disambiguationData":[OSD([sQuery(id+"F10.wireOp",EDGE,"E80.top"),sQuery(id+"F10.wireOp",EDGE,"E80.right")])]})});
            fillet(context, id + "F12", {"entities" : qUnion([Q0, Q1, Q2, Q3]), "radius" : 5 * mm, "tangentPropagation" : true, "allowEdgeOverflow" : false});
        }
    });
